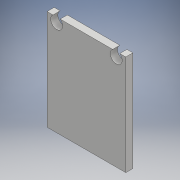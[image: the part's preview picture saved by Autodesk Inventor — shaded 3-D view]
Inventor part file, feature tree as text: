
AUTODESK INVENTOR PART (.ipt)
format: ipt  version: 2017 (Build 210142000, 142)  size: 121,856 bytes
history: native  units: mm
features: other x3, extrude x1, sketch x1
ambient origin geometry x8: Origin, YZ Plane, XZ Plane, XY Plane, X Axis, Y Axis, Z Axis, Center Point
bodies: Solid1 (feature_tree)
feature tree (5):
  other  "k2_t2_base.ipt"
  extrude  "Extrusion4"  Depth=10.0mm
  other  "Solid1::k2_t2_base.ipt"
  other  "TaggingFeature1"
  sketch  "Sketch4"  dims[d17=10.0mm d22=17.0mm d23=10.0mm d24=0.0mm d44=12.0mm d45=5.0mm d46=5.0mm d47=4.0mm d48=4.0mm d49=2.0mm d50=2.0mm]
